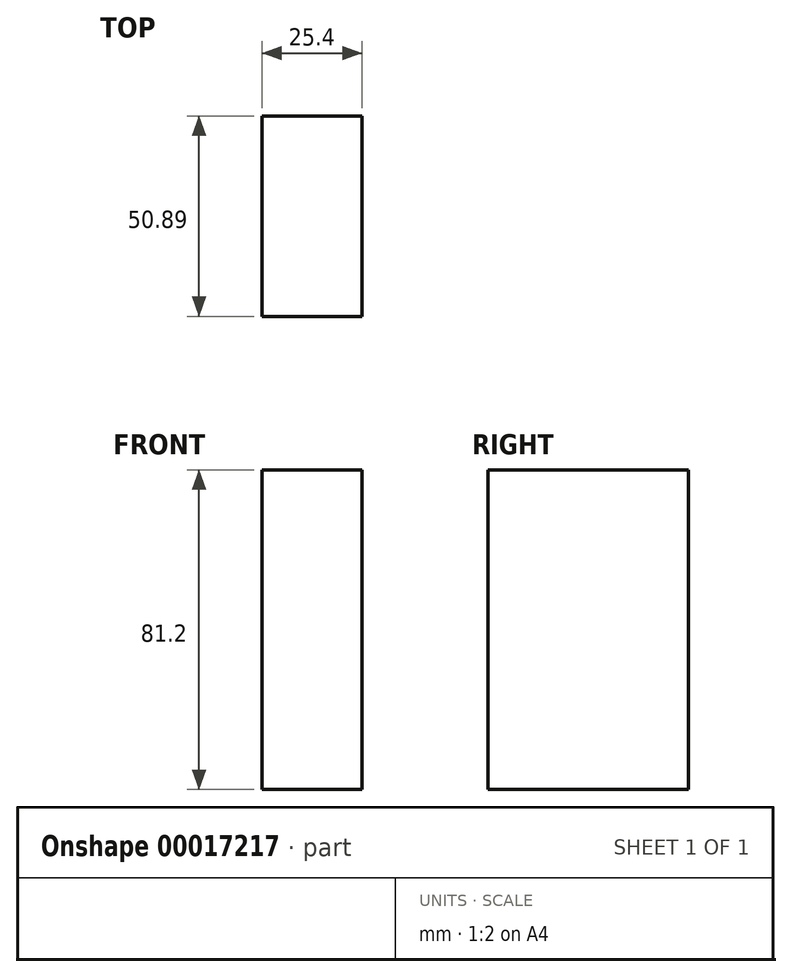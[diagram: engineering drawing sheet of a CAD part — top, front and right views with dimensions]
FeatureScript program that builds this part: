
annotation { "Feature Type Name" : "Feature", "Feature Type Description" : "" }
export const myFeature = defineFeature(function(context is Context, id is Id, definition is map)
    precondition{}
    {
        {
            var Q0;
            Q0=qCreatedBy(makeId("Right.planeOp"),FACE);
            var sketch = newSketch(context, id + "F0", { "sketchPlane" : qUnion([Q0])});
            skLineSegment(sketch, "E0.bottom", {"start": v(-57.16, 35.5) * mm, "end": v(-6.27, 35.5) * mm});
            skLineSegment(sketch, "E0.top", {"start": v(-57.16, -45.7) * mm, "end": v(-6.27, -45.7) * mm});
            skLineSegment(sketch, "E0.left", {"start": v(-57.16, 35.5) * mm, "end": v(-57.16, -45.7) * mm});
            skLineSegment(sketch, "E0.right", {"start": v(-6.27, 35.5) * mm, "end": v(-6.27, -45.7) * mm});
            skSolve(sketch);
        }
        {
            var Q0;
            Q0=makeQuery(id+"F0.imprint","IMPRINT",FACE,{"disambiguationData":[TD([[makeQuery(id+"F0.imprint","IMPRINT",EDGE,{"derivedFrom":sQuery(id+"F0.wireOp",EDGE,"E0.bottom")}),-1.0]])]});
            extrude(context, id + "F1", {"entities" : qUnion([Q0]), "endBound" : BoundingType.SYMMETRIC, "depth" : 25.4 * mm});
        }
    });
